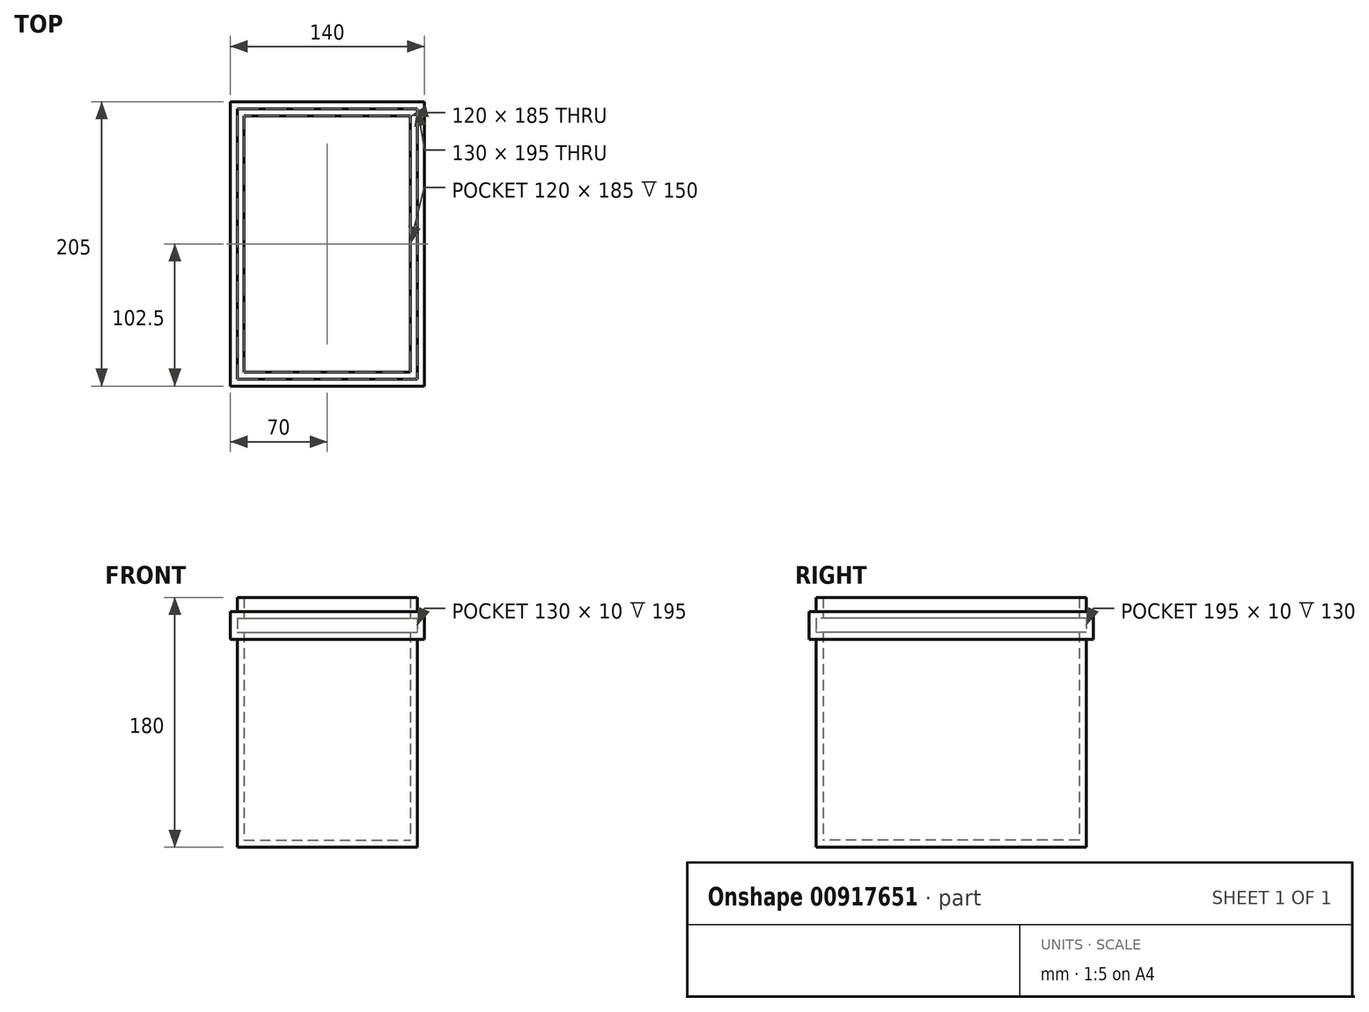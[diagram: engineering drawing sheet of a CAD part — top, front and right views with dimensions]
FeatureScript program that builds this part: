
annotation { "Feature Type Name" : "Feature", "Feature Type Description" : "" }
export const myFeature = defineFeature(function(context is Context, id is Id, definition is map)
    precondition{}
    {
        {
            var Q0;
            Q0=qCreatedBy(makeId("Top.planeOp"),FACE);
            var sketch = newSketch(context, id + "F0", { "sketchPlane" : qUnion([Q0])});
            skLineSegment(sketch, "E0.bottom", {"start": v(-65, 97.5) * mm, "end": v(65, 97.5) * mm});
            skLineSegment(sketch, "E0.top", {"start": v(-65, -97.5) * mm, "end": v(65, -97.5) * mm});
            skLineSegment(sketch, "E0.left", {"start": v(-65, 97.5) * mm, "end": v(-65, -97.5) * mm});
            skLineSegment(sketch, "E0.right", {"start": v(65, 97.5) * mm, "end": v(65, -97.5) * mm});
            skPoint(sketch, "E0.middle", {"position": v(0, 0) * mm});
            skSolve(sketch);
        }
        {
            var Q0;
            Q0=makeQuery(id+"F0.imprint","IMPRINT",FACE,{"disambiguationData":[TD([[makeQuery(id+"F0.imprint","IMPRINT",EDGE,{"derivedFrom":sQuery(id+"F0.wireOp",EDGE,"E0.bottom")}),-1.0]])]});
            var sketch = newSketch(context, id + "F1", { "sketchPlane" : qUnion([Q0])});
            skLineSegment(sketch, "E1.0", {"start": v(-70, 102.5) * mm, "end": v(-70, -102.5) * mm});
            skLineSegment(sketch, "E1.1", {"start": v(-70, 102.5) * mm, "end": v(70, 102.5) * mm});
            skLineSegment(sketch, "E1.2", {"start": v(70, 102.5) * mm, "end": v(70, -102.5) * mm});
            skLineSegment(sketch, "E1.3", {"start": v(-70, -102.5) * mm, "end": v(70, -102.5) * mm});
            skSolve(sketch);
        }
        {
            var Q0;
            Q0 = qSketchRegion(id + "F0", true);
            extrude(context, id + "F2", {"entities" : qUnion([Q0]), "depth" : 180 * mm, "offsetDistance" : 25 * mm});
        }
        {
            var Q0;
            Q0 = qSketchRegion(id + "F1", true);
            extrude(context, id + "F3", {"entities" : qUnion([Q0]), "operationType" : NewBodyOperationType.ADD, "depth" : 170 * mm, "offsetDistance" : 25 * mm, "hasSecondDirection" : true, "secondDirectionOppositeDirection" : false, "secondDirectionDepth" : 150 * mm});
        }
        {
            var Q0;
            Q0=makeQuery(id+"F2.opExtrude","CAP_FACE",FACE,{"disambiguationData":[OSD([sQuery(id+"F0.wireOp",EDGE,"E0.bottom"),sQuery(id+"F0.wireOp",EDGE,"E0.top"),sQuery(id+"F0.wireOp",EDGE,"E0.left"),sQuery(id+"F0.wireOp",EDGE,"E0.right")])],"isStart":false});
            shell(context, id + "F4", {"entities" : qUnion([Q0]), "thickness" : 5 * mm});
        }
    });
